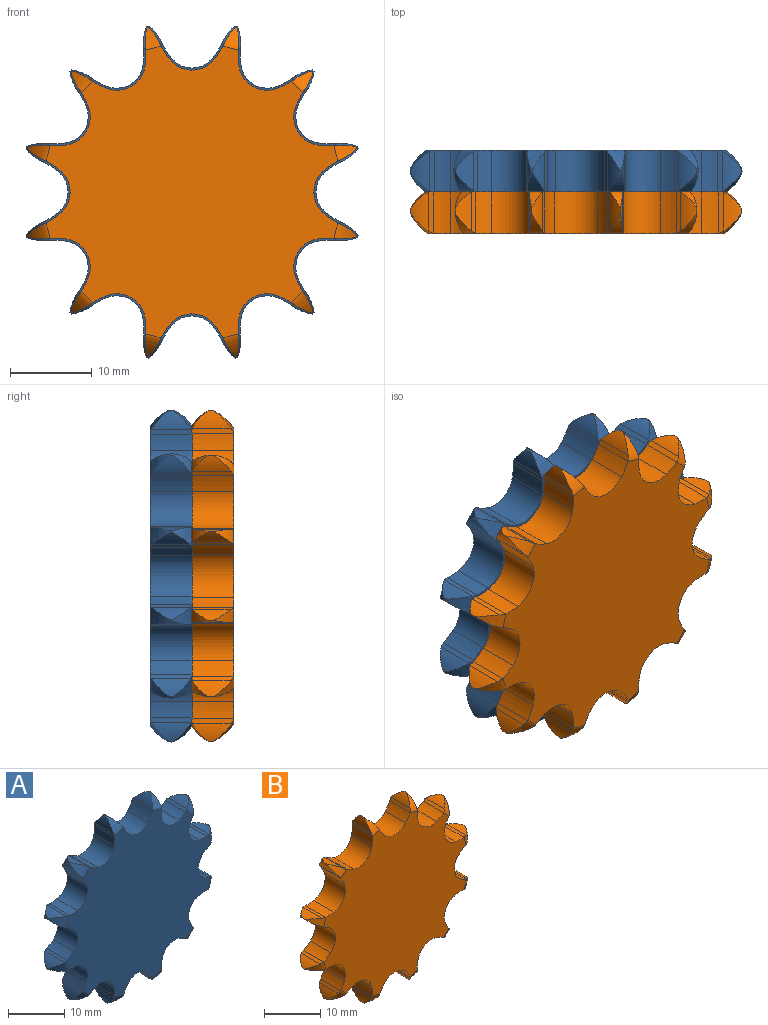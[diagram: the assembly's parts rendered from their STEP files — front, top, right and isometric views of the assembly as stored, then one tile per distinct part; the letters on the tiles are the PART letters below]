
ASSEMBLY  parts=2 mates=1
PART A: 122 faces, bbox 42.1x5.2x42.1 mm
  f0: cylinder r=21mm len=0.25mm, axis (0,-1,0), area 0mm2, adj f14,f26,f40,f115
  f1: cylinder r=21mm len=0.18mm, axis (0,-1,0), area 0mm2, adj f15,f27,f109,f121
  f2: cylinder r=21mm len=0.25mm, axis (0,-1,0), area 0mm2, adj f16,f28,f102,f110
  f3: cylinder r=21mm len=0.25mm, axis (0,-1,0), area 0mm2, adj f17,f29,f95,f103
  f4: cylinder r=21mm len=0.18mm, axis (0,-1,0), area 0mm2, adj f18,f30,f88,f96
  f5: cylinder r=21mm len=0.25mm, axis (0,-1,0), area 0mm2, adj f19,f31,f81,f89
  f6: cylinder r=21mm len=0.25mm, axis (0,-1,0), area 0mm2, adj f20,f32,f74,f82
  f7: cylinder r=21mm len=0.18mm, axis (0,-1,0), area 0mm2, adj f21,f33,f67,f75
  f8: cylinder r=21mm len=0.25mm, axis (0,-1,0), area 0mm2, adj f22,f34,f60,f68
  f9: cylinder r=21mm len=0.25mm, axis (0,-1,0), area 0mm2, adj f23,f35,f53,f61
  f10: cylinder r=21mm len=0.18mm, axis (0,-1,0), area 0mm2, adj f24,f36,f46,f54
  f11: cylinder r=21mm len=0.25mm, axis (0,-1,0), area 0mm2, adj f25,f37,f39,f47
  f12: plane 36.32x36.32mm, normal (0,-1,0), area 871.4mm2, adj f14,f15,f16,f17,f18,f19,f20,f21
  f13: plane 36.32x36.32mm, normal (0,1,0), area 871.4mm2, adj f26,f27,f28,f29,f30,f31,f32,f33
  f14: bspline ~13.33x4.84mm, area 5.1mm2, adj f0,f12,f40,f41,f115,f116
  f15: bspline ~15.61x15.61mm, area 5.1mm2, adj f1,f12,f108,f109,f120,f121
  f16: bspline ~13.33x4.84mm, area 5.1mm2, adj f2,f12,f101,f102,f110,f111
  f17: bspline ~13.33x4.84mm, area 5.1mm2, adj f3,f12,f94,f95,f103,f104
  f18: bspline ~15.61x15.61mm, area 5.1mm2, adj f4,f12,f87,f88,f96,f97
  f19: bspline ~10.58x4.84mm, area 5.1mm2, adj f5,f12,f80,f81,f89,f90
  f20: bspline ~10.58x4.84mm, area 5.1mm2, adj f6,f12,f73,f74,f82,f83
  f21: bspline ~15.61x15.61mm, area 5.1mm2, adj f7,f12,f66,f67,f75,f76
  f22: bspline ~13.33x4.84mm, area 5.1mm2, adj f8,f12,f59,f60,f68,f69
  f23: bspline ~13.33x4.84mm, area 5.1mm2, adj f9,f12,f52,f53,f61,f62
  f24: bspline ~15.61x15.61mm, area 5.1mm2, adj f10,f12,f45,f46,f54,f55
  f25: bspline ~13.33x4.84mm, area 5.1mm2, adj f11,f12,f38,f39,f47,f48
  f26: bspline ~13.33x4.84mm, area 5.1mm2, adj f0,f13,f40,f41,f115,f116
  f27: bspline ~15.61x15.61mm, area 5.1mm2, adj f1,f13,f108,f109,f120,f121
  f28: bspline ~13.33x4.84mm, area 5.1mm2, adj f2,f13,f101,f102,f110,f111
  f29: bspline ~13.33x4.84mm, area 5.1mm2, adj f3,f13,f94,f95,f103,f104
  f30: bspline ~15.61x15.61mm, area 5.1mm2, adj f4,f13,f87,f88,f96,f97
  f31: bspline ~10.58x4.84mm, area 5.1mm2, adj f5,f13,f80,f81,f89,f90
  f32: bspline ~10.58x4.84mm, area 5.1mm2, adj f6,f13,f73,f74,f82,f83
  f33: bspline ~15.61x15.61mm, area 5.1mm2, adj f7,f13,f66,f67,f75,f76
  f34: bspline ~13.33x4.84mm, area 5.1mm2, adj f8,f13,f59,f60,f68,f69
  f35: bspline ~13.33x4.84mm, area 5.1mm2, adj f9,f13,f52,f53,f61,f62
  f36: bspline ~15.61x15.61mm, area 5.1mm2, adj f10,f13,f45,f46,f54,f55
  f37: bspline ~13.33x4.84mm, area 5.1mm2, adj f11,f13,f38,f39,f47,f48
  f38: plane 5.19x0.65mm, normal (-0.89,0,0.45), area 3.2mm2, adj f12,f13,f25,f37,f39,f44
  f39: cylinder r=5.34mm len=4.84mm, axis (0,-1,0), area 7mm2, adj f11,f25,f37,f38
  f40: cylinder r=5.34mm len=4.84mm, axis (0,-1,0), area 7mm2, adj f0,f14,f26,f41
  f41: plane 5.19x0.65mm, normal (0.89,0,0.45), area 3.2mm2, adj f12,f13,f14,f26,f40,f42
  f42: cylinder r=8.31mm len=5.1mm, axis (0,-1,0), area 9.9mm2, adj f12,f13,f41,f43
  f43: cylinder r=3.23mm len=5.1mm, axis (0,-1,0), area 28.7mm2, adj f12,f13,f42,f44
  f44: cylinder r=8.31mm len=5.1mm, axis (0,-1,0), area 9.9mm2, adj f12,f13,f38,f43
  f45: plane 5.19x0.62mm, normal (-0.55,0,0.84), area 3.2mm2, adj f12,f13,f24,f36,f46,f51
  f46: cylinder r=5.34mm len=4.85mm, axis (0,-1,0), area 7mm2, adj f10,f24,f36,f45
  f47: cylinder r=5.34mm len=4.85mm, axis (0,-1,0), area 7mm2, adj f11,f25,f37,f48
  f48: plane 5.19x0.72mm, normal (1,0,-0.06), area 3.2mm2, adj f12,f13,f25,f37,f47,f49
  f49: cylinder r=8.31mm len=5.1mm, axis (0,-1,0), area 9.9mm2, adj f12,f13,f48,f50
  f50: cylinder r=3.23mm len=5.1mm, axis (0,-1,0), area 28.7mm2, adj f12,f13,f49,f51
  f51: cylinder r=8.31mm len=5.1mm, axis (0,-1,0), area 9.9mm2, adj f12,f13,f45,f50
  f52: plane 5.19x0.72mm, normal (-0.06,0,1), area 3.2mm2, adj f12,f13,f23,f35,f53,f58
  f53: cylinder r=5.34mm len=4.85mm, axis (0,-1,0), area 7mm2, adj f9,f23,f35,f52
  f54: cylinder r=5.34mm len=4.85mm, axis (0,-1,0), area 7mm2, adj f10,f24,f36,f55
  f55: plane 5.19x0.62mm, normal (0.84,0,-0.55), area 3.2mm2, adj f12,f13,f24,f36,f54,f56
  f56: cylinder r=8.31mm len=5.1mm, axis (0,-1,0), area 9.9mm2, adj f12,f13,f55,f57
  f57: cylinder r=3.23mm len=5.1mm, axis (0,-1,0), area 28.7mm2, adj f12,f13,f56,f58
  f58: cylinder r=8.31mm len=5.1mm, axis (0,-1,0), area 9.9mm2, adj f12,f13,f52,f57
  f59: plane 5.19x0.65mm, normal (0.45,0,0.89), area 3.2mm2, adj f12,f13,f22,f34,f60,f65
  f60: cylinder r=5.34mm len=4.84mm, axis (0,-1,0), area 7mm2, adj f8,f22,f34,f59
  f61: cylinder r=5.34mm len=4.84mm, axis (0,-1,0), area 7mm2, adj f9,f23,f35,f62
  f62: plane 5.19x0.65mm, normal (0.45,0,-0.89), area 3.2mm2, adj f12,f13,f23,f35,f61,f63
  f63: cylinder r=8.31mm len=5.1mm, axis (0,-1,0), area 9.9mm2, adj f12,f13,f62,f64
  f64: cylinder r=3.23mm len=5.1mm, axis (0,-1,0), area 28.7mm2, adj f12,f13,f63,f65
  f65: cylinder r=8.31mm len=5.1mm, axis (0,-1,0), area 9.9mm2, adj f12,f13,f59,f64
  f66: plane 5.19x0.62mm, normal (0.84,0,0.55), area 3.2mm2, adj f12,f13,f21,f33,f67,f72
  f67: cylinder r=5.34mm len=4.85mm, axis (0,-1,0), area 7mm2, adj f7,f21,f33,f66
  f68: cylinder r=5.34mm len=4.85mm, axis (0,-1,0), area 7mm2, adj f8,f22,f34,f69
  f69: plane 5.19x0.72mm, normal (-0.06,0,-1), area 3.2mm2, adj f12,f13,f22,f34,f68,f70
  f70: cylinder r=8.31mm len=5.1mm, axis (0,-1,0), area 9.9mm2, adj f12,f13,f69,f71
  f71: cylinder r=3.23mm len=5.1mm, axis (0,-1,0), area 28.7mm2, adj f12,f13,f70,f72
  f72: cylinder r=8.31mm len=5.1mm, axis (0,-1,0), area 9.9mm2, adj f12,f13,f66,f71
  f73: plane 5.19x0.72mm, normal (1,0,0.06), area 3.2mm2, adj f12,f13,f20,f32,f74,f79
  f74: cylinder r=5.34mm len=4.85mm, axis (0,-1,0), area 7mm2, adj f6,f20,f32,f73
  f75: cylinder r=5.34mm len=4.85mm, axis (0,-1,0), area 7mm2, adj f7,f21,f33,f76
  f76: plane 5.19x0.62mm, normal (-0.55,0,-0.84), area 3.2mm2, adj f12,f13,f21,f33,f75,f77
  f77: cylinder r=8.31mm len=5.1mm, axis (0,-1,0), area 9.9mm2, adj f12,f13,f76,f78
  f78: cylinder r=3.23mm len=5.1mm, axis (0,-1,0), area 28.7mm2, adj f12,f13,f77,f79
  f79: cylinder r=8.31mm len=5.1mm, axis (0,-1,0), area 9.9mm2, adj f12,f13,f73,f78
  f80: plane 5.19x0.65mm, normal (0.89,0,-0.45), area 3.2mm2, adj f12,f13,f19,f31,f81,f86
  f81: cylinder r=5.34mm len=4.84mm, axis (0,-1,0), area 7mm2, adj f5,f19,f31,f80
  f82: cylinder r=5.34mm len=4.84mm, axis (0,-1,0), area 7mm2, adj f6,f20,f32,f83
  f83: plane 5.19x0.65mm, normal (-0.89,0,-0.45), area 3.2mm2, adj f12,f13,f20,f32,f82,f84
  f84: cylinder r=8.31mm len=5.1mm, axis (0,-1,0), area 9.9mm2, adj f12,f13,f83,f85
  f85: cylinder r=3.23mm len=5.1mm, axis (0,-1,0), area 28.7mm2, adj f12,f13,f84,f86
  f86: cylinder r=8.31mm len=5.1mm, axis (0,-1,0), area 9.9mm2, adj f12,f13,f80,f85
  f87: plane 5.19x0.62mm, normal (0.55,0,-0.84), area 3.2mm2, adj f12,f13,f18,f30,f88,f93
  f88: cylinder r=5.34mm len=4.85mm, axis (0,-1,0), area 7mm2, adj f4,f18,f30,f87
  f89: cylinder r=5.34mm len=4.85mm, axis (0,-1,0), area 7mm2, adj f5,f19,f31,f90
  f90: plane 5.19x0.72mm, normal (-1,0,0.06), area 3.2mm2, adj f12,f13,f19,f31,f89,f91
  f91: cylinder r=8.31mm len=5.1mm, axis (0,-1,0), area 9.9mm2, adj f12,f13,f90,f92
  f92: cylinder r=3.23mm len=5.1mm, axis (0,-1,0), area 28.7mm2, adj f12,f13,f91,f93
  f93: cylinder r=8.31mm len=5.1mm, axis (0,-1,0), area 9.9mm2, adj f12,f13,f87,f92
  f94: plane 5.19x0.72mm, normal (0.06,0,-1), area 3.2mm2, adj f12,f13,f17,f29,f95,f100
  f95: cylinder r=5.34mm len=4.85mm, axis (0,-1,0), area 7mm2, adj f3,f17,f29,f94
  f96: cylinder r=5.34mm len=4.85mm, axis (0,-1,0), area 7mm2, adj f4,f18,f30,f97
  f97: plane 5.19x0.62mm, normal (-0.84,0,0.55), area 3.2mm2, adj f12,f13,f18,f30,f96,f98
  f98: cylinder r=8.31mm len=5.1mm, axis (0,-1,0), area 9.9mm2, adj f12,f13,f97,f99
  f99: cylinder r=3.23mm len=5.1mm, axis (0,-1,0), area 28.7mm2, adj f12,f13,f98,f100
  f100: cylinder r=8.31mm len=5.1mm, axis (0,-1,0), area 9.9mm2, adj f12,f13,f94,f99
  f101: plane 5.19x0.65mm, normal (-0.45,0,-0.89), area 3.2mm2, adj f12,f13,f16,f28,f102,f107
  f102: cylinder r=5.34mm len=4.84mm, axis (0,-1,0), area 7mm2, adj f2,f16,f28,f101
  f103: cylinder r=5.34mm len=4.84mm, axis (0,-1,0), area 7mm2, adj f3,f17,f29,f104
  f104: plane 5.19x0.65mm, normal (-0.45,0,0.89), area 3.2mm2, adj f12,f13,f17,f29,f103,f105
  f105: cylinder r=8.31mm len=5.1mm, axis (0,-1,0), area 9.9mm2, adj f12,f13,f104,f106
  f106: cylinder r=3.23mm len=5.1mm, axis (0,-1,0), area 28.7mm2, adj f12,f13,f105,f107
  f107: cylinder r=8.31mm len=5.1mm, axis (0,-1,0), area 9.9mm2, adj f12,f13,f101,f106
  f108: plane 5.19x0.62mm, normal (-0.84,0,-0.55), area 3.2mm2, adj f12,f13,f15,f27,f109,f114
  f109: cylinder r=5.34mm len=4.85mm, axis (0,-1,0), area 7mm2, adj f1,f15,f27,f108
  f110: cylinder r=5.34mm len=4.85mm, axis (0,-1,0), area 7mm2, adj f2,f16,f28,f111
  f111: plane 5.19x0.72mm, normal (0.06,0,1), area 3.2mm2, adj f12,f13,f16,f28,f110,f112
  f112: cylinder r=8.31mm len=5.1mm, axis (0,-1,0), area 9.9mm2, adj f12,f13,f111,f113
  f113: cylinder r=3.23mm len=5.1mm, axis (0,-1,0), area 28.7mm2, adj f12,f13,f112,f114
  f114: cylinder r=8.31mm len=5.1mm, axis (0,-1,0), area 9.9mm2, adj f12,f13,f108,f113
  f115: cylinder r=5.34mm len=4.85mm, axis (0,-1,0), area 7mm2, adj f0,f14,f26,f116
  f116: plane 5.19x0.72mm, normal (-1,0,-0.06), area 3.2mm2, adj f12,f13,f14,f26,f115,f117
  f117: cylinder r=8.31mm len=5.1mm, axis (0,-1,0), area 9.9mm2, adj f12,f13,f116,f118
  f118: cylinder r=3.23mm len=5.1mm, axis (0,-1,0), area 28.7mm2, adj f12,f13,f117,f119
  f119: cylinder r=8.31mm len=5.1mm, axis (0,-1,0), area 9.9mm2, adj f12,f13,f118,f120
  f120: plane 5.19x0.62mm, normal (0.55,0,0.84), area 3.2mm2, adj f12,f13,f15,f27,f119,f121
  f121: cylinder r=5.34mm len=4.85mm, axis (0,-1,0), area 7mm2, adj f1,f15,f27,f120
PART B: 110 faces, bbox 42x5.1x42 mm
  f0: bspline ~15.55x15.55mm, area 2.8mm2, adj f12,f17,f18,f19,f20
  f1: bspline ~10.58x4.62mm, area 2.8mm2, adj f12,f24,f25,f26,f27
  f2: bspline ~10.58x4.62mm, area 2.8mm2, adj f12,f31,f32,f33,f34
  f3: bspline ~15.55x15.55mm, area 2.8mm2, adj f12,f38,f39,f40,f41
  f4: bspline ~13.33x4.62mm, area 2.8mm2, adj f12,f45,f46,f47,f48
  f5: bspline ~13.33x4.62mm, area 2.8mm2, adj f12,f52,f53,f54,f55
  f6: bspline ~15.55x15.55mm, area 2.8mm2, adj f12,f59,f60,f61,f62
  f7: bspline ~13.33x4.62mm, area 2.8mm2, adj f12,f66,f67,f68,f69
  f8: bspline ~13.33x4.62mm, area 2.8mm2, adj f12,f73,f74,f75,f76
  f9: bspline ~15.55x15.55mm, area 2.8mm2, adj f12,f80,f81,f82,f83
  f10: bspline ~13.33x4.62mm, area 2.8mm2, adj f12,f87,f88,f89,f90
  f11: bspline ~13.33x4.62mm, area 2.8mm2, adj f12,f13,f94,f95,f96
  f12: plane 36.65x36.65mm, normal (0,1,0), area 844.8mm2, adj f0,f1,f2,f3,f4,f5,f6,f7
  f13: plane 5.13x0.71mm, normal (0.06,0,-1), area 3.4mm2, adj f11,f12,f14,f96,f107
  f14: cylinder r=8.97mm len=5.1mm, axis (0,-1,0), area 10.6mm2, adj f12,f13,f15,f107,f108
  f15: cylinder r=3.48mm len=5.1mm, axis (0,-1,0), area 31mm2, adj f12,f14,f16,f108
  f16: cylinder r=8.97mm len=5.1mm, axis (0,-1,0), area 10.6mm2, adj f12,f15,f17,f97,f108
  f17: plane 5.13x0.6mm, normal (-0.84,0,0.55), area 3.4mm2, adj f0,f12,f16,f18,f97
  f18: cylinder r=5.77mm len=4.74mm, axis (0,-1,0), area 5.8mm2, adj f0,f17,f19,f97
  f19: cylinder r=5.77mm len=4.74mm, axis (0,-1,0), area 5.8mm2, adj f0,f18,f20,f97
  f20: plane 5.13x0.6mm, normal (0.55,0,-0.84), area 3.4mm2, adj f0,f12,f19,f21,f97
  f21: cylinder r=8.97mm len=5.1mm, axis (0,-1,0), area 10.6mm2, adj f12,f20,f22,f97,f108
  f22: cylinder r=3.48mm len=5.1mm, axis (0,-1,0), area 31mm2, adj f12,f21,f23,f108
  f23: cylinder r=8.97mm len=5.1mm, axis (0,-1,0), area 10.6mm2, adj f12,f22,f24,f98,f108
  f24: plane 5.13x0.71mm, normal (-1,0,0.06), area 3.4mm2, adj f1,f12,f23,f25,f98
  f25: cylinder r=5.77mm len=4.74mm, axis (0,-1,0), area 5.8mm2, adj f1,f24,f26,f98
  f26: cylinder r=5.77mm len=4.74mm, axis (0,-1,0), area 5.8mm2, adj f1,f25,f27,f98
  f27: plane 5.13x0.64mm, normal (0.89,0,-0.45), area 3.4mm2, adj f1,f12,f26,f28,f98
  f28: cylinder r=8.97mm len=5.1mm, axis (0,-1,0), area 10.6mm2, adj f12,f27,f29,f98,f108
  f29: cylinder r=3.48mm len=5.34mm, axis (0,-1,0), area 31mm2, adj f12,f28,f30,f108
  f30: cylinder r=8.97mm len=5.1mm, axis (0,-1,0), area 10.6mm2, adj f12,f29,f31,f99,f108
  f31: plane 5.13x0.64mm, normal (-0.89,0,-0.45), area 3.4mm2, adj f2,f12,f30,f32,f99
  f32: cylinder r=5.77mm len=4.74mm, axis (0,-1,0), area 5.8mm2, adj f2,f31,f33,f99
  f33: cylinder r=5.77mm len=4.74mm, axis (0,-1,0), area 5.8mm2, adj f2,f32,f34,f99
  f34: plane 5.13x0.71mm, normal (1,0,0.06), area 3.4mm2, adj f2,f12,f33,f35,f99
  f35: cylinder r=8.97mm len=5.1mm, axis (0,-1,0), area 10.6mm2, adj f12,f34,f36,f99,f108
  f36: cylinder r=3.48mm len=5.1mm, axis (0,-1,0), area 31mm2, adj f12,f35,f37,f108
  f37: cylinder r=8.97mm len=5.1mm, axis (0,-1,0), area 10.6mm2, adj f12,f36,f38,f100,f108
  f38: plane 5.13x0.6mm, normal (-0.55,0,-0.84), area 3.4mm2, adj f3,f12,f37,f39,f100
  f39: cylinder r=5.77mm len=4.74mm, axis (0,-1,0), area 5.8mm2, adj f3,f38,f40,f100
  f40: cylinder r=5.77mm len=4.74mm, axis (0,-1,0), area 5.8mm2, adj f3,f39,f41,f100
  f41: plane 5.13x0.6mm, normal (0.84,0,0.55), area 3.4mm2, adj f3,f12,f40,f42,f100
  f42: cylinder r=8.97mm len=5.1mm, axis (0,-1,0), area 10.6mm2, adj f12,f41,f43,f100,f108
  f43: cylinder r=3.48mm len=5.1mm, axis (0,-1,0), area 31mm2, adj f12,f42,f44,f108
  f44: cylinder r=8.97mm len=5.1mm, axis (0,-1,0), area 10.6mm2, adj f12,f43,f45,f101,f108
  f45: plane 5.13x0.71mm, normal (-0.06,0,-1), area 3.4mm2, adj f4,f12,f44,f46,f101
  f46: cylinder r=5.77mm len=4.74mm, axis (0,-1,0), area 5.8mm2, adj f4,f45,f47,f101
  f47: cylinder r=5.77mm len=4.74mm, axis (0,-1,0), area 5.8mm2, adj f4,f46,f48,f101
  f48: plane 5.13x0.64mm, normal (0.45,0,0.89), area 3.4mm2, adj f4,f12,f47,f49,f101
  f49: cylinder r=8.97mm len=5.1mm, axis (0,-1,0), area 10.6mm2, adj f12,f48,f50,f101,f108
  f50: cylinder r=3.48mm len=5.34mm, axis (0,-1,0), area 31mm2, adj f12,f49,f51,f108
  f51: cylinder r=8.97mm len=5.1mm, axis (0,-1,0), area 10.6mm2, adj f12,f50,f52,f102,f108
  f52: plane 5.13x0.64mm, normal (0.45,0,-0.89), area 3.4mm2, adj f5,f12,f51,f53,f102
  f53: cylinder r=5.77mm len=4.74mm, axis (0,-1,0), area 5.8mm2, adj f5,f52,f54,f102
  f54: cylinder r=5.77mm len=4.74mm, axis (0,-1,0), area 5.8mm2, adj f5,f53,f55,f102
  f55: plane 5.13x0.71mm, normal (-0.06,0,1), area 3.4mm2, adj f5,f12,f54,f56,f102
  f56: cylinder r=8.97mm len=5.1mm, axis (0,-1,0), area 10.6mm2, adj f12,f55,f57,f102,f108
  f57: cylinder r=3.48mm len=5.1mm, axis (0,-1,0), area 31mm2, adj f12,f56,f58,f108
  f58: cylinder r=8.97mm len=5.1mm, axis (0,-1,0), area 10.6mm2, adj f12,f57,f59,f103,f108
  f59: plane 5.13x0.6mm, normal (0.84,0,-0.55), area 3.4mm2, adj f6,f12,f58,f60,f103
  f60: cylinder r=5.77mm len=4.74mm, axis (0,-1,0), area 5.8mm2, adj f6,f59,f61,f103
  f61: cylinder r=5.77mm len=4.74mm, axis (0,-1,0), area 5.8mm2, adj f6,f60,f62,f103
  f62: plane 5.13x0.6mm, normal (-0.55,0,0.84), area 3.4mm2, adj f6,f12,f61,f63,f103
  f63: cylinder r=8.97mm len=5.1mm, axis (0,-1,0), area 10.6mm2, adj f12,f62,f64,f103,f108
  f64: cylinder r=3.48mm len=5.1mm, axis (0,-1,0), area 31mm2, adj f12,f63,f65,f108
  f65: cylinder r=8.97mm len=5.1mm, axis (0,-1,0), area 10.6mm2, adj f12,f64,f66,f104,f108
  f66: plane 5.13x0.71mm, normal (1,0,-0.06), area 3.4mm2, adj f7,f12,f65,f67,f104
  f67: cylinder r=5.77mm len=4.74mm, axis (0,-1,0), area 5.8mm2, adj f7,f66,f68,f104
  f68: cylinder r=5.77mm len=4.74mm, axis (0,-1,0), area 5.8mm2, adj f7,f67,f69,f104
  f69: plane 5.13x0.64mm, normal (-0.89,0,0.45), area 3.4mm2, adj f7,f12,f68,f70,f104
  f70: cylinder r=8.97mm len=5.1mm, axis (0,-1,0), area 10.6mm2, adj f12,f69,f71,f104,f108
  f71: cylinder r=3.48mm len=5.34mm, axis (0,-1,0), area 31mm2, adj f12,f70,f72,f108
  f72: cylinder r=8.97mm len=5.1mm, axis (0,-1,0), area 10.6mm2, adj f12,f71,f73,f105,f108
  f73: plane 5.13x0.64mm, normal (0.89,0,0.45), area 3.4mm2, adj f8,f12,f72,f74,f105
  f74: cylinder r=5.77mm len=4.74mm, axis (0,-1,0), area 5.8mm2, adj f8,f73,f75,f105
  f75: cylinder r=5.77mm len=4.74mm, axis (0,-1,0), area 5.8mm2, adj f8,f74,f76,f105
  f76: plane 5.13x0.71mm, normal (-1,0,-0.06), area 3.4mm2, adj f8,f12,f75,f77,f105
  f77: cylinder r=8.97mm len=5.1mm, axis (0,-1,0), area 10.6mm2, adj f12,f76,f78,f105,f108
  f78: cylinder r=3.48mm len=5.1mm, axis (0,-1,0), area 31mm2, adj f12,f77,f79,f108
  f79: cylinder r=8.97mm len=5.1mm, axis (0,-1,0), area 10.6mm2, adj f12,f78,f80,f106,f108
  f80: plane 5.13x0.6mm, normal (0.55,0,0.84), area 3.4mm2, adj f9,f12,f79,f81,f106
  f81: cylinder r=5.77mm len=4.74mm, axis (0,-1,0), area 5.8mm2, adj f9,f80,f82,f106
  f82: cylinder r=5.77mm len=4.74mm, axis (0,-1,0), area 5.8mm2, adj f9,f81,f83,f106
  f83: plane 5.13x0.6mm, normal (-0.84,0,-0.55), area 3.4mm2, adj f9,f12,f82,f84,f106
  f84: cylinder r=8.97mm len=5.1mm, axis (0,-1,0), area 10.6mm2, adj f12,f83,f85,f106,f108
  f85: cylinder r=3.48mm len=5.1mm, axis (0,-1,0), area 31mm2, adj f12,f84,f86,f108
  f86: cylinder r=8.97mm len=5.1mm, axis (0,-1,0), area 10.6mm2, adj f12,f85,f87,f108,f109
  f87: plane 5.13x0.71mm, normal (0.06,0,1), area 3.4mm2, adj f10,f12,f86,f88,f109
  f88: cylinder r=5.77mm len=4.74mm, axis (0,-1,0), area 5.8mm2, adj f10,f87,f89,f109
  f89: cylinder r=5.77mm len=4.74mm, axis (0,-1,0), area 5.8mm2, adj f10,f88,f90,f109
  f90: plane 5.13x0.64mm, normal (-0.45,0,-0.89), area 3.4mm2, adj f10,f12,f89,f91,f109
  f91: cylinder r=8.97mm len=5.1mm, axis (0,-1,0), area 10.6mm2, adj f12,f90,f92,f108,f109
  f92: cylinder r=3.48mm len=5.34mm, axis (0,-1,0), area 31mm2, adj f12,f91,f93,f108
  f93: cylinder r=8.97mm len=5.1mm, axis (0,-1,0), area 10.6mm2, adj f12,f92,f94,f107,f108
  f94: plane 5.13x0.64mm, normal (-0.45,0,0.89), area 3.4mm2, adj f11,f12,f93,f95,f107
  f95: cylinder r=5.77mm len=4.74mm, axis (0,-1,0), area 5.8mm2, adj f11,f94,f96,f107
  f96: cylinder r=5.77mm len=4.74mm, axis (0,-1,0), area 5.8mm2, adj f11,f13,f95,f107
  f97: bspline ~15.68x15.68mm, area 4mm2, adj f16,f17,f18,f19,f20,f21,f108
  f98: bspline ~10.58x5.05mm, area 4mm2, adj f23,f24,f25,f26,f27,f28,f108
  f99: bspline ~10.58x5.05mm, area 4mm2, adj f30,f31,f32,f33,f34,f35,f108
  f100: bspline ~15.68x15.68mm, area 4mm2, adj f37,f38,f39,f40,f41,f42,f108
  f101: bspline ~13.33x5.05mm, area 4mm2, adj f44,f45,f46,f47,f48,f49,f108
  f102: bspline ~13.33x5.05mm, area 4mm2, adj f51,f52,f53,f54,f55,f56,f108
  f103: bspline ~15.68x15.68mm, area 4mm2, adj f58,f59,f60,f61,f62,f63,f108
  f104: bspline ~13.33x5.05mm, area 4mm2, adj f65,f66,f67,f68,f69,f70,f108
  f105: bspline ~13.33x5.05mm, area 4mm2, adj f72,f73,f74,f75,f76,f77,f108
  f106: bspline ~15.68x15.68mm, area 4mm2, adj f79,f80,f81,f82,f83,f84,f108
  f107: bspline ~13.33x5.05mm, area 4mm2, adj f13,f14,f93,f94,f95,f96,f108
  f108: plane 35.73x35.73mm, normal (0,-1,0), area 833.9mm2, adj f14,f15,f16,f21,f22,f23,f28,f29
  f109: bspline ~13.33x5.05mm, area 4mm2, adj f86,f87,f88,f89,f90,f91,f108
PLACE A t=(6.54,5.96,7.1)mm
PLACE B t=(6.54,0.86,7.1)mm
MATE fastened B.f12 <-> A.f0  axis (0,1,0) through (6.54,5.96,7.1)mm
